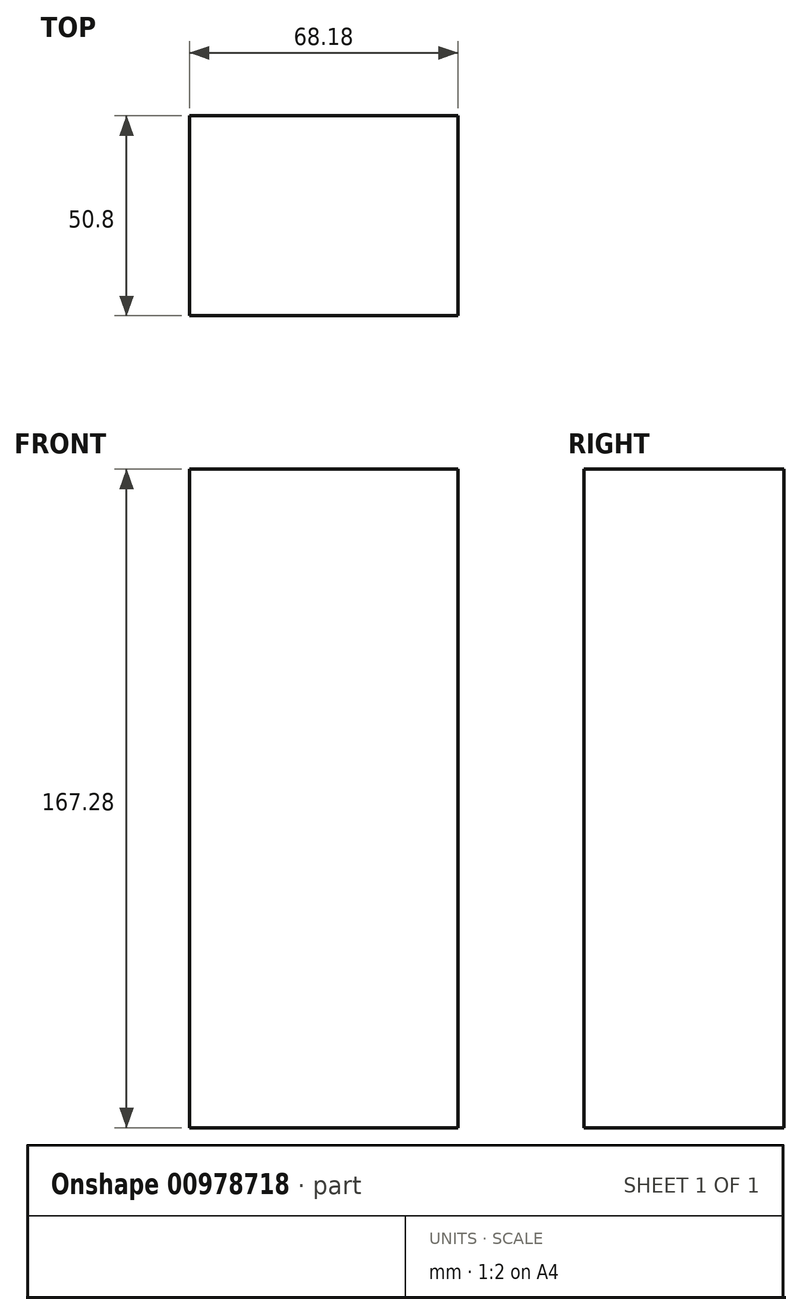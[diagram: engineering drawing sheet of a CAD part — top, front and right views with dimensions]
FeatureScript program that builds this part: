
annotation { "Feature Type Name" : "Feature", "Feature Type Description" : "" }
export const myFeature = defineFeature(function(context is Context, id is Id, definition is map)
    precondition{}
    {
        {
            var Q0;
            Q0=qCreatedBy(makeId("Front.planeOp"),FACE);
            var sketch = newSketch(context, id + "F0", { "sketchPlane" : qUnion([Q0])});
            skLineSegment(sketch, "E0.bottom", {"start": v(-21.39, 83.64) * mm, "end": v(21.39, 83.64) * mm});
            skLineSegment(sketch, "E0.top", {"start": v(-21.39, -83.64) * mm, "end": v(21.39, -83.64) * mm});
            skLineSegment(sketch, "E0.left", {"start": v(-21.39, 83.64) * mm, "end": v(-21.39, -83.64) * mm});
            skLineSegment(sketch, "E0.right", {"start": v(21.39, 83.64) * mm, "end": v(21.39, -83.64) * mm});
            skPoint(sketch, "E0.middle", {"position": v(0, 0) * mm});
            skSolve(sketch);
        }
        {
            var Q0;
            Q0 = qSketchRegion(id + "F0", true);
            extrude(context, id + "F1", {"entities" : qUnion([Q0]), "oppositeDirection" : true, "depth" : 50.8 * mm, "offsetDistance" : 25.4 * mm});
        }
        {
            var Q0;
            Q0=makeQuery(id+"F1.opExtrude","SWEPT_FACE",FACE,{"disambiguationData":[OSD([sQuery(id+"F0.wireOp",EDGE,"E0.left")])]});
            extrude(context, id + "F2", {"entities" : qUnion([Q0]), "operationType" : NewBodyOperationType.ADD, "depth" : 25.4 * mm, "offsetDistance" : 25.4 * mm});
        }
    });
